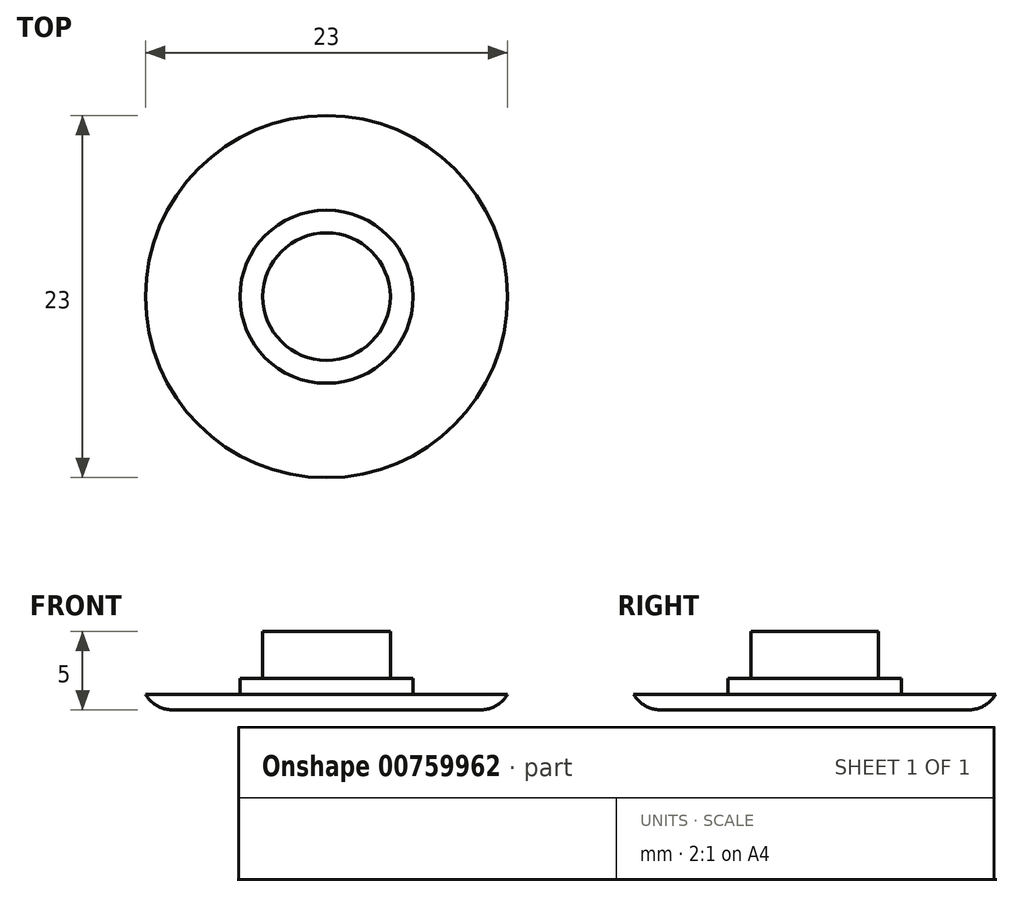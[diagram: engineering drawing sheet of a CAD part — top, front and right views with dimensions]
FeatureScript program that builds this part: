
annotation { "Feature Type Name" : "Feature", "Feature Type Description" : "" }
export const myFeature = defineFeature(function(context is Context, id is Id, definition is map)
    precondition{}
    {
        {
            var Q0;
            Q0=qCreatedBy(makeId("Top.planeOp"),FACE);
            var sketch = newSketch(context, id + "F0", { "sketchPlane" : qUnion([Q0])});
            skCircle(sketch, "E0", {"center": v(0, 0) * mm, "radius": 11.5 * mm});
            skCircle(sketch, "E1", {"center": v(0, 0) * mm, "radius": 4.05 * mm});
            skCircle(sketch, "E2", {"center": v(0, 0) * mm, "radius": 5.5 * mm});
            skCircle(sketch, "E3", {"center": v(0, 0) * mm, "radius": 2 * mm});
            skSolve(sketch);
        }
        {
            var Q0;
            Q0=makeQuery(id+"F0.imprint","IMPRINT",FACE,{"disambiguationData":[TD([[makeQuery(id+"F0.imprint","IMPRINT",EDGE,{"derivedFrom":sQuery(id+"F0.wireOp",EDGE,"E0")}),1.0]])]});
            extrude(context, id + "F1", {"entities" : qUnion([Q0]), "depth" : 1 * mm, "offsetDistance" : 25 * mm});
        }
        {
            var Q0;
            Q0=makeQuery(id+"F0.imprint","IMPRINT",FACE,{"disambiguationData":[TD([[makeQuery(id+"F0.imprint","IMPRINT",EDGE,{"derivedFrom":sQuery(id+"F0.wireOp",EDGE,"E1")}),-1.0]])]});
            extrude(context, id + "F2", {"entities" : qUnion([Q0]), "operationType" : NewBodyOperationType.ADD, "depth" : 2 * mm, "offsetDistance" : 25 * mm});
        }
        {
            var Q0;
            Q0=makeQuery(id+"F0.imprint","IMPRINT",FACE,{"disambiguationData":[TD([[makeQuery(id+"F0.imprint","IMPRINT",EDGE,{"derivedFrom":sQuery(id+"F0.wireOp",EDGE,"E1")}),1.0]])]});
            var Q1;
            Q1=makeQuery(id+"F0.imprint","IMPRINT",FACE,{"disambiguationData":[TD([[makeQuery(id+"F0.imprint","IMPRINT",EDGE,{"derivedFrom":sQuery(id+"F0.wireOp",EDGE,"E3")}),1.0]])]});
            extrude(context, id + "F3", {"entities" : qUnion([Q0, Q1]), "operationType" : NewBodyOperationType.ADD, "depth" : 5 * mm, "offsetDistance" : 25 * mm});
        }
        {
            var Q0;
            Q0=makeQuery(id+"F1.opExtrude","CAP_EDGE",EDGE,{"disambiguationData":[OSD([sQuery(id+"F0.wireOp",EDGE,"E0")])],"isStart":true});
            fillet(context, id + "F4", {"entities" : qUnion([Q0]), "radius" : 2 * mm, "tangentPropagation" : true, "allowEdgeOverflow" : false});
        }
    });
